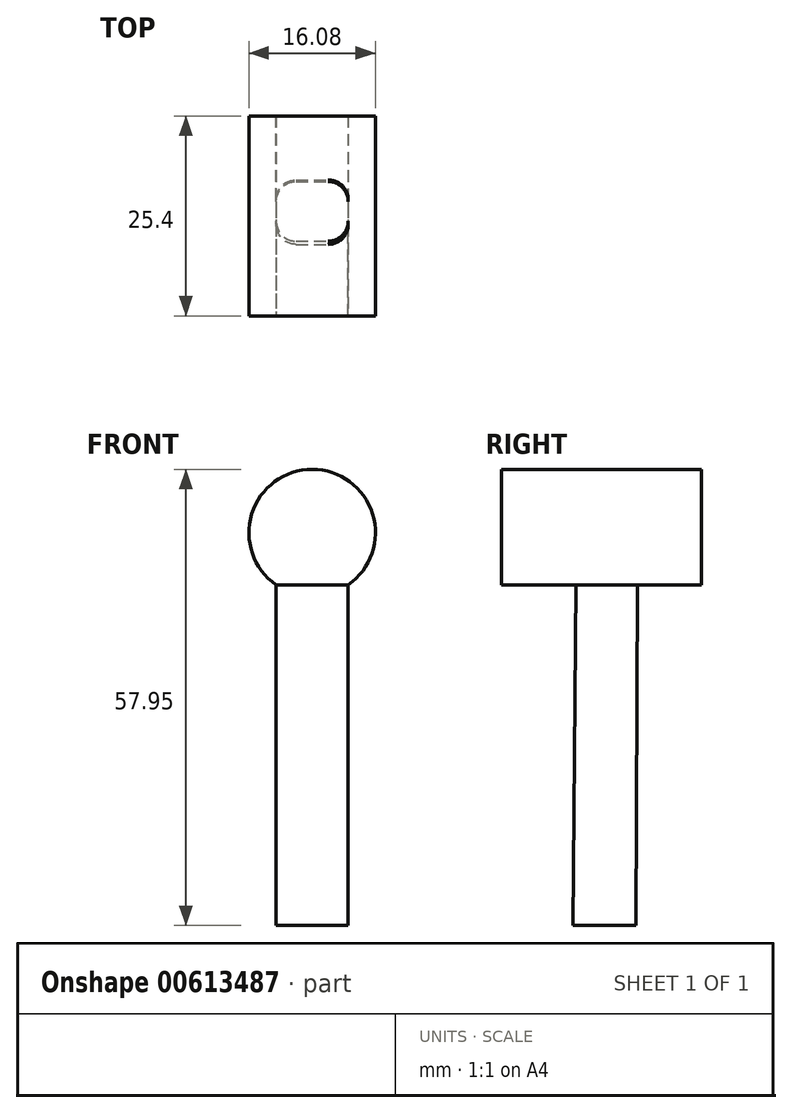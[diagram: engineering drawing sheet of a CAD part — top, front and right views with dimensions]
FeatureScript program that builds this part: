
annotation { "Feature Type Name" : "Feature", "Feature Type Description" : "" }
export const myFeature = defineFeature(function(context is Context, id is Id, definition is map)
    precondition{}
    {
        {
            var Q0;
            Q0=qCreatedBy(makeId("Front.planeOp"),FACE);
            var sketch = newSketch(context, id + "F0", { "sketchPlane" : qUnion([Q0])});
            skLineSegment(sketch, "E0", {"start": v(0, 0) * mm, "end": v(-25.4, 0) * mm});
            skLineSegment(sketch, "E1", {"start": v(-25.4, 0) * mm, "end": v(-25.4, 63.5) * mm});
            skLineSegment(sketch, "E2", {"start": v(-25.4, 63.5) * mm, "end": v(0, 63.5) * mm});
            skLineSegment(sketch, "E3", {"start": v(0, 63.5) * mm, "end": v(0, 0) * mm});
            skSolve(sketch);
        }
        {
            var Q0;
            Q0 = qSketchRegion(id + "F0", true);
            extrude(context, id + "F1", {"entities" : qUnion([Q0]), "depth" : 25.4 * mm, "offsetDistance" : 25.4 * mm});
        }
        {
            var Q0;
            Q0=makeQuery(id+"F1.opExtrude","CAP_FACE",FACE,{"disambiguationData":[OSD([sQuery(id+"F0.wireOp",EDGE,"E0"),sQuery(id+"F0.wireOp",EDGE,"E1"),sQuery(id+"F0.wireOp",EDGE,"E2"),sQuery(id+"F0.wireOp",EDGE,"E3")])],"isStart":false});
            var sketch = newSketch(context, id + "F2", { "sketchPlane" : qUnion([Q0])});
            skLineSegment(sketch, "E4", {"start": v(-16.83, 43.73) * mm, "end": v(-7.67, 43.73) * mm});
            skLineSegment(sketch, "E5", {"start": v(-7.67, 43.73) * mm, "end": v(-7.67, 0) * mm});
            skLineSegment(sketch, "E6", {"start": v(-7.67, 0) * mm, "end": v(-16.83, 0) * mm});
            skLineSegment(sketch, "E7", {"start": v(-16.83, 0) * mm, "end": v(-16.83, 43.73) * mm});
            skCircle(sketch, "E8", {"center": v(-12.25, 49.9) * mm, "radius": 8.04 * mm});
            skPoint(sketch, "E8.centerSnap0", {"position": v(-12.25, 43.73) * mm});
            skSolve(sketch);
        }
        {
            var Q0;
            {var subQ0=makeQuery(id+"F1.opExtrude","CAP_EDGE",EDGE,{"disambiguationData":[OSD([sQuery(id+"F0.wireOp",EDGE,"E1")])],"isStart":false});Q0=makeQuery(id+"F2.imprint","IMPRINT",FACE,{"disambiguationData":[TD([[makeQuery(id+"F2.imprint","IMPRINT",EDGE,{"derivedFrom":subQ0}),-1.0]])]});}
            extrude(context, id + "F3", {"entities" : qUnion([Q0]), "operationType" : NewBodyOperationType.REMOVE, "oppositeDirection" : true, "depth" : 25.4 * mm, "offsetDistance" : 25.4 * mm});
        }
        {
            var Q0;
            Q0=qCreatedBy(makeId("Right.planeOp"),FACE);
            var sketch = newSketch(context, id + "F4", { "sketchPlane" : qUnion([Q0])});
            skLineSegment(sketch, "E9", {"start": v(-8.13, 43.27) * mm, "end": v(5.84, 43.27) * mm});
            skLineSegment(sketch, "E10", {"start": v(5.84, 43.27) * mm, "end": v(5.84, -3.66) * mm});
            skLineSegment(sketch, "E11", {"start": v(5.84, -3.66) * mm, "end": v(-8.36, -3.66) * mm});
            skLineSegment(sketch, "E12", {"start": v(-8.36, -3.66) * mm, "end": v(-8.13, 43.27) * mm});
            skLineSegment(sketch, "E13", {"start": v(-17.97, 43.04) * mm, "end": v(-18.2, -3.9) * mm});
            skLineSegment(sketch, "E14", {"start": v(-18.2, -3.9) * mm, "end": v(-37.65, -3.8) * mm});
            skPoint(sketch, "E15.start.orphan", {"position": v(-29.42, 42.12) * mm});
            skPoint(sketch, "E16.end.orphan", {"position": v(-37.65, 42.12) * mm});
            skLineSegment(sketch, "E17", {"start": v(-37.65, -3.8) * mm, "end": v(-37.65, 42.12) * mm});
            skLineSegment(sketch, "E18", {"start": v(-17.97, 43.04) * mm, "end": v(-37.65, 43.13) * mm});
            skSolve(sketch);
        }
        {
            var Q0;
            Q0 = qSketchRegion(id + "F4", true);
            extrude(context, id + "F5", {"entities" : qUnion([Q0]), "operationType" : NewBodyOperationType.REMOVE, "oppositeDirection" : true, "depth" : 25.4 * mm, "offsetDistance" : 25.4 * mm});
        }
        {
            var Q0;
            Q0=qCreatedBy(makeId("Right.planeOp"),FACE);
            var sketch = newSketch(context, id + "F6", { "sketchPlane" : qUnion([Q0])});
            skLineSegment(sketch, "E19", {"start": v(-15.91, 43.27) * mm, "end": v(-32.62, 43.27) * mm});
            skLineSegment(sketch, "E20", {"start": v(-32.62, 43.27) * mm, "end": v(-32.62, -6.4) * mm});
            skLineSegment(sketch, "E21", {"start": v(-32.62, -6.4) * mm, "end": v(-16.37, -6.4) * mm});
            skLineSegment(sketch, "E22", {"start": v(-16.37, -6.4) * mm, "end": v(-15.91, 43.27) * mm});
            skSolve(sketch);
        }
        {
            var Q0;
            Q0 = qSketchRegion(id + "F6", true);
            extrude(context, id + "F7", {"entities" : qUnion([Q0]), "operationType" : NewBodyOperationType.REMOVE, "oppositeDirection" : true, "depth" : 25.4 * mm, "offsetDistance" : 25.4 * mm});
        }
        {
            var Q0;
            Q0=makeQuery(id+"F5.boolean.opBoolean","INTERSECT",EDGE,{"derivedFrom":[makeQuery(id+"F3.boolean.opBoolean","COPY",FACE,{"derivedFrom":makeQuery(id+"F3.opExtrude","SWEPT_FACE",FACE,{"disambiguationData":[OSD([sQuery(id+"F2.wireOp",EDGE,"E7")])]})}),makeQuery(id+"F5.opExtrude","SWEPT_FACE",FACE,{"disambiguationData":[OSD([sQuery(id+"F4.wireOp",EDGE,"E12")])]})]});
            var Q1;
            Q1=makeQuery(id+"F7.boolean.opBoolean","INTERSECT",EDGE,{"derivedFrom":[makeQuery(id+"F3.boolean.opBoolean","COPY",FACE,{"derivedFrom":makeQuery(id+"F3.opExtrude","SWEPT_FACE",FACE,{"disambiguationData":[OSD([sQuery(id+"F2.wireOp",EDGE,"E7")])]})}),makeQuery(id+"F7.opExtrude","SWEPT_FACE",FACE,{"disambiguationData":[OSD([sQuery(id+"F6.wireOp",EDGE,"E22")])]})]});
            var Q2;
            Q2=makeQuery(id+"F7.boolean.opBoolean","INTERSECT",EDGE,{"derivedFrom":[makeQuery(id+"F3.boolean.opBoolean","COPY",FACE,{"derivedFrom":makeQuery(id+"F3.opExtrude","SWEPT_FACE",FACE,{"disambiguationData":[OSD([sQuery(id+"F2.wireOp",EDGE,"E5")])]})}),makeQuery(id+"F7.opExtrude","SWEPT_FACE",FACE,{"disambiguationData":[OSD([sQuery(id+"F6.wireOp",EDGE,"E22")])]})]});
            var Q3;
            Q3=makeQuery(id+"F5.boolean.opBoolean","INTERSECT",EDGE,{"derivedFrom":[makeQuery(id+"F3.boolean.opBoolean","COPY",FACE,{"derivedFrom":makeQuery(id+"F3.opExtrude","SWEPT_FACE",FACE,{"disambiguationData":[OSD([sQuery(id+"F2.wireOp",EDGE,"E5")])]})}),makeQuery(id+"F5.opExtrude","SWEPT_FACE",FACE,{"disambiguationData":[OSD([sQuery(id+"F4.wireOp",EDGE,"E12")])]})]});
            var Q4;
            Q4=makeQuery(id+"F3.boolean.opBoolean","COPY",EDGE,{"derivedFrom":makeQuery(id+"F3.opExtrude","CAP_EDGE",EDGE,{"disambiguationData":[OSD([sQuery(id+"F2.wireOp",EDGE,"E8")])],"isStart":true})});
            var Q5;
            Q5=makeQuery(id+"F3.boolean.opBoolean","COPY",EDGE,{"derivedFrom":makeQuery(id+"F3.opExtrude","CAP_EDGE",EDGE,{"disambiguationData":[OSD([sQuery(id+"F2.wireOp",EDGE,"E8")])],"isStart":false})});
            fillet(context, id + "F8", {"entities" : qUnion([Q0, Q1, Q2, Q3, Q4, Q5]), "radius" : 2.54 * mm, "tangentPropagation" : true, "allowEdgeOverflow" : false});
        }
    });
